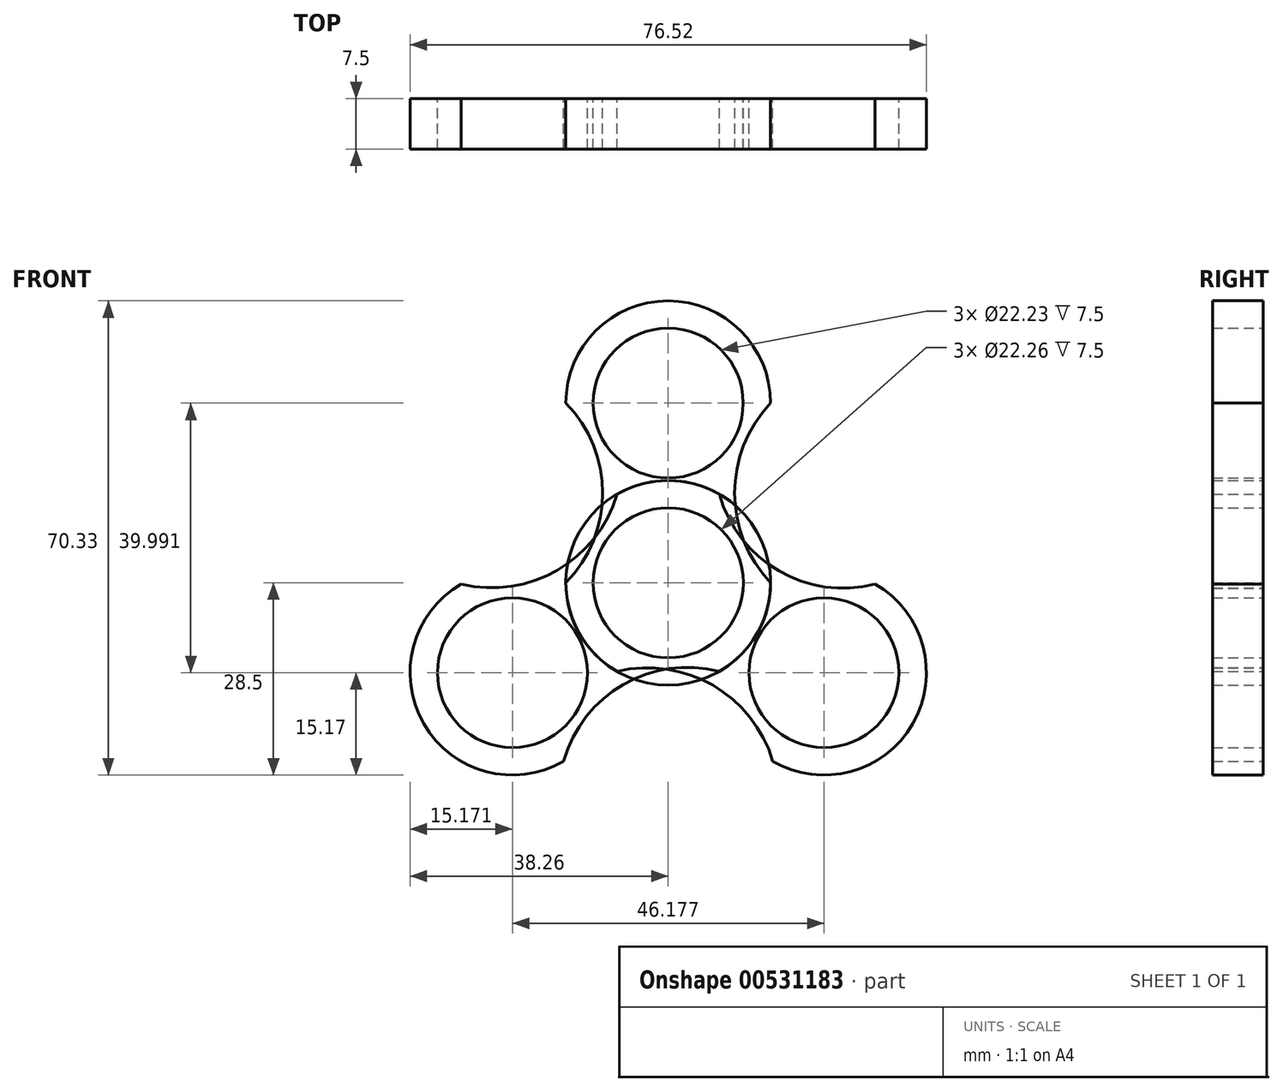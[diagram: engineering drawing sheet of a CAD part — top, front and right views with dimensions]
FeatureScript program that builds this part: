
annotation { "Feature Type Name" : "Feature", "Feature Type Description" : "" }
export const myFeature = defineFeature(function(context is Context, id is Id, definition is map)
    precondition{}
    {
        {
            var Q0;
            Q0=qCreatedBy(makeId("Front.planeOp"),FACE);
            var sketch = newSketch(context, id + "F0", { "sketchPlane" : qUnion([Q0])});
            skCircle(sketch, "E0", {"center": v(0, 0) * mm, "radius": 11.13 * mm});
            skArc(sketch, "E1", {"start": v(9.94, 11.46) * mm, "mid": v(0.09, 15.17) * mm, "end": v(-9.81, 11.57) * mm});
            skLineSegment(sketch, "E2", {"start": v(-15.17, 26.66) * mm, "end": v(15.17, 26.66) * mm});
            skArc(sketch, "E3", {"start": v(-15.17, 0) * mm, "mid": v(-9.73, 13.33) * mm, "end": v(-15.17, 26.66) * mm});
            skArc(sketch, "E4", {"start": v(15.17, 26.66) * mm, "mid": v(9.85, 13.33) * mm, "end": v(15.17, 0) * mm});
            skPoint(sketch, "E5.center.orphan", {"position": v(0, 26.66) * mm});
            skArc(sketch, "E6.trimOffspring", {"start": v(15.17, 26.66) * mm, "mid": v(0, 41.83) * mm, "end": v(-15.17, 26.66) * mm});
            skArc(sketch, "E7.trimOffspring", {"start": v(-15.17, 0) * mm, "mid": v(0, -15.17) * mm, "end": v(15.17, 0) * mm});
            skCircle(sketch, "E8", {"center": v(0, 26.66) * mm, "radius": 11.11 * mm});
            skSolve(sketch);
        }
        {
            var Q0;
            {var subQ0=sQuery(id+"F0.wireOp",EDGE,"E6.trimOffspring");Q0=makeQuery(id+"F0.imprint","IMPRINT",FACE,{"disambiguationData":[TD([[makeQuery(id+"F0.imprint","IMPRINT",EDGE,{"derivedFrom":subQ0}),1.0]])]});}
            var Q1;
            {var subQ9=sQuery(id+"F0.wireOp",EDGE,"E1");Q1=makeQuery(id+"F0.imprint","IMPRINT",FACE,{"disambiguationData":[TD([[makeQuery(id+"F0.imprint","IMPRINT",EDGE,{"derivedFrom":subQ9}),-1.0]])]});}
            var Q2;
            Q2=makeQuery(id+"F0.imprint","IMPRINT",FACE,{"disambiguationData":[TD([[makeQuery(id+"F0.imprint","IMPRINT",EDGE,{"derivedFrom":sQuery(id+"F0.wireOp",EDGE,"E0")}),-1.0]])]});
            extrude(context, id + "F1", {"entities" : qUnion([Q0, Q1, Q2]), "depth" : 7.5 * mm, "offsetDistance" : 25 * mm});
        }
        {
            var Q0;
            Q0=makeQuery(id+"F1.opExtrude","SWEPT_BODY",BODY,{"disambiguationData":[OSD([sQuery(id+"F0.wireOp",EDGE,"E0"),sQuery(id+"F0.wireOp",EDGE,"E3"),sQuery(id+"F0.wireOp",EDGE,"E4"),sQuery(id+"F0.wireOp",EDGE,"E6.trimOffspring"),sQuery(id+"F0.wireOp",EDGE,"E7.trimOffspring"),sQuery(id+"F0.wireOp",EDGE,"E8")])]});
            var Q1;
            Q1=makeQuery(id+"F1.opExtrude","CAP_EDGE",EDGE,{"disambiguationData":[OSD([sQuery(id+"F0.wireOp",EDGE,"E0")])],"isStart":false});
            transform(context, id + "F2", {"entities" : qUnion([Q0]), "transformType" : TransformType.ROTATION, "transformAxis" : qUnion([Q1]), "angle" : 120 * degree, "makeCopy" : true});
        }
        {
            var Q0;
            Q0=makeQuery(id+"F1.opExtrude","SWEPT_BODY",BODY,{"disambiguationData":[OSD([sQuery(id+"F0.wireOp",EDGE,"E0"),sQuery(id+"F0.wireOp",EDGE,"E3"),sQuery(id+"F0.wireOp",EDGE,"E4"),sQuery(id+"F0.wireOp",EDGE,"E6.trimOffspring"),sQuery(id+"F0.wireOp",EDGE,"E7.trimOffspring"),sQuery(id+"F0.wireOp",EDGE,"E8")])]});
            var Q1;
            Q1=makeQuery(id+"F1.opExtrude","CAP_EDGE",EDGE,{"disambiguationData":[OSD([sQuery(id+"F0.wireOp",EDGE,"E0")])],"isStart":false});
            transform(context, id + "F3", {"entities" : qUnion([Q0]), "transformType" : TransformType.ROTATION, "transformAxis" : qUnion([Q1]), "angle" : 120 * degree, "oppositeDirection" : true, "makeCopy" : true});
        }
    });
